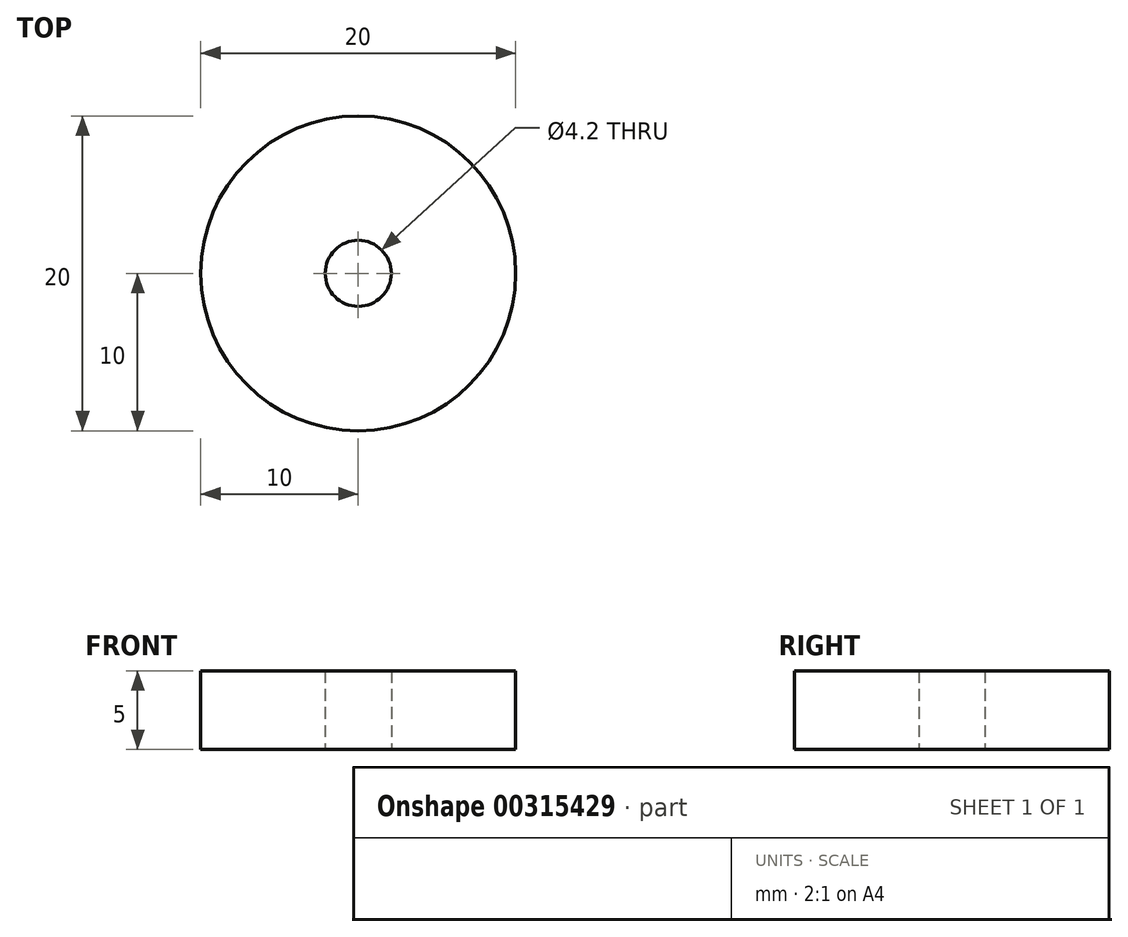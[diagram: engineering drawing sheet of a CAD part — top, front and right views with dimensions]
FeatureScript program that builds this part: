
annotation { "Feature Type Name" : "Feature", "Feature Type Description" : "" }
export const myFeature = defineFeature(function(context is Context, id is Id, definition is map)
    precondition{}
    {
        {
            var Q0;
            Q0=qCreatedBy(makeId("Top.planeOp"),FACE);
            var sketch = newSketch(context, id + "F0", { "sketchPlane" : qUnion([Q0])});
            skCircle(sketch, "E0", {"center": v(0, 0) * mm, "radius": 2.1 * mm});
            skCircle(sketch, "E1", {"center": v(0, 0) * mm, "radius": 10 * mm});
            skSolve(sketch);
        }
        {
            var Q0;
            Q0=makeQuery(id+"F0.imprint","IMPRINT",FACE,{"disambiguationData":[TD([[makeQuery(id+"F0.imprint","IMPRINT",EDGE,{"derivedFrom":sQuery(id+"F0.wireOp",EDGE,"E0")}),-1.0]])]});
            extrude(context, id + "F1", {"entities" : qUnion([Q0]), "depth" : 5 * mm});
        }
    });
